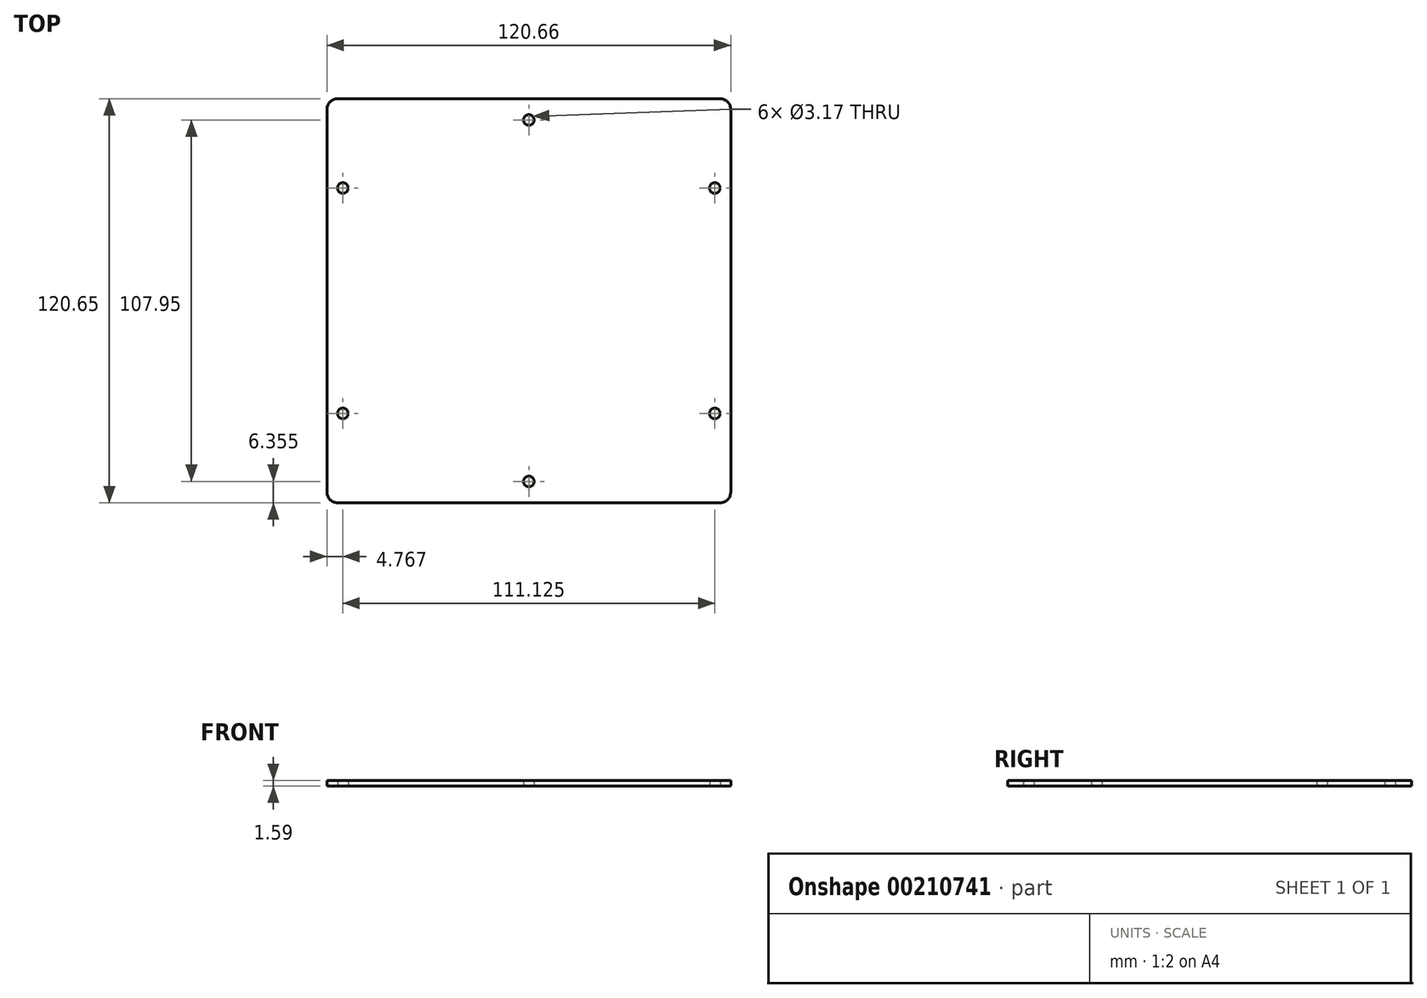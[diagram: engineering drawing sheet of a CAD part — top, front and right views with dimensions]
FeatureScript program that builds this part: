
annotation { "Feature Type Name" : "Feature", "Feature Type Description" : "" }
export const myFeature = defineFeature(function(context is Context, id is Id, definition is map)
    precondition{}
    {
        {
            var Q0;
            Q0=qCreatedBy(makeId("Top.planeOp"),FACE);
            var sketch = newSketch(context, id + "F0", { "sketchPlane" : qUnion([Q0])});
            skLineSegment(sketch, "E0.bottom", {"start": v(-57.15, 60.32) * mm, "end": v(57.15, 60.33) * mm});
            skLineSegment(sketch, "E0.top", {"start": v(-57.15, -60.33) * mm, "end": v(57.15, -60.32) * mm});
            skLineSegment(sketch, "E0.left", {"start": v(-60.33, 57.15) * mm, "end": v(-60.32, -57.15) * mm});
            skLineSegment(sketch, "E0.right", {"start": v(60.32, 57.15) * mm, "end": v(60.33, -57.15) * mm});
            skPoint(sketch, "E1.visualSharp", {"position": v(-60.33, 60.32) * mm});
            skArc(sketch, "E1.filletArc", {"start": v(-57.15, 60.32) * mm, "mid": v(-59.4, 59.4) * mm, "end": v(-60.33, 57.15) * mm});
            skPoint(sketch, "E2.visualSharp", {"position": v(60.32, 60.33) * mm});
            skArc(sketch, "E2.filletArc", {"start": v(60.33, 57.15) * mm, "mid": v(59.4, 59.4) * mm, "end": v(57.15, 60.33) * mm});
            skPoint(sketch, "E3.visualSharp", {"position": v(60.33, -60.32) * mm});
            skArc(sketch, "E3.filletArc", {"start": v(57.15, -60.32) * mm, "mid": v(59.4, -59.4) * mm, "end": v(60.32, -57.15) * mm});
            skPoint(sketch, "E4.visualSharp", {"position": v(-60.32, -60.33) * mm});
            skArc(sketch, "E4.filletArc", {"start": v(-60.32, -57.15) * mm, "mid": v(-59.4, -59.4) * mm, "end": v(-57.15, -60.32) * mm});
            skCircle(sketch, "E5", {"center": v(55.56, 33.66) * mm, "radius": 1.59 * mm});
            skCircle(sketch, "E6", {"center": v(55.56, -33.65) * mm, "radius": 1.59 * mm});
            skCircle(sketch, "E7", {"center": v(-55.56, -33.66) * mm, "radius": 1.59 * mm});
            skCircle(sketch, "E8", {"center": v(-55.56, 33.65) * mm, "radius": 1.59 * mm});
            skCircle(sketch, "E9", {"center": v(0, -53.98) * mm, "radius": 1.59 * mm});
            skCircle(sketch, "E10", {"center": v(0, 53.98) * mm, "radius": 1.59 * mm});
            skSolve(sketch);
        }
        {
            var Q0;
            Q0 = qSketchRegion(id + "F0", true);
            extrude(context, id + "F1", {"entities" : qUnion([Q0]), "depth" : 1.59 * mm});
        }
    });
